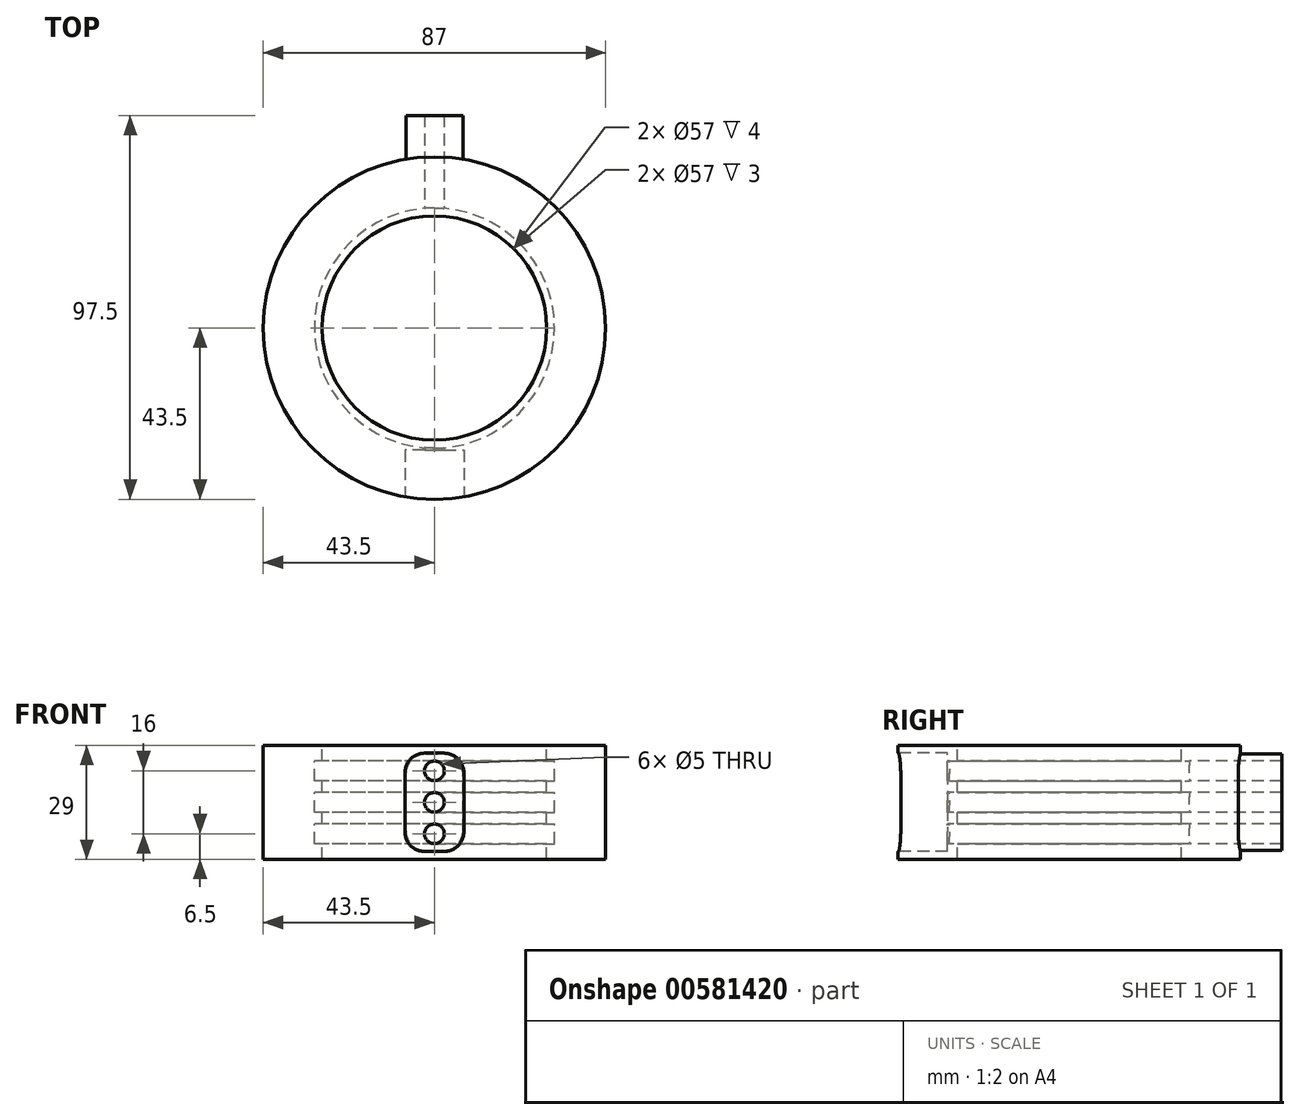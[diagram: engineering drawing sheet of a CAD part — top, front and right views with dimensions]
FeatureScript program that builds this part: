
annotation { "Feature Type Name" : "Feature", "Feature Type Description" : "" }
export const myFeature = defineFeature(function(context is Context, id is Id, definition is map)
    precondition{}
    {
        {
            var Q0;
            Q0=qCreatedBy(makeId("Front.planeOp"),FACE);
            var sketch = newSketch(context, id + "F0", { "sketchPlane" : qUnion([Q0])});
            skLineSegment(sketch, "E0.bottom", {"start": v(28.5, 14.5) * mm, "end": v(43.5, 14.5) * mm});
            skLineSegment(sketch, "E0.top", {"start": v(28.5, -14.5) * mm, "end": v(43.5, -14.5) * mm});
            skLineSegment(sketch, "E0.left", {"start": v(28.5, 14.5) * mm, "end": v(28.5, 10.5) * mm});
            skLineSegment(sketch, "E0.right", {"start": v(43.5, 14.5) * mm, "end": v(43.5, -14.5) * mm});
            skLineSegment(sketch, "E1", {"start": v(0, 16.26) * mm, "end": v(0, -13.74) * mm});
            skLineSegment(sketch, "E2", {"start": v(28.5, -14.5) * mm, "end": v(28.5, -10.5) * mm});
            skLineSegment(sketch, "E3", {"start": v(28.5, 2.5) * mm, "end": v(30.5, 2.5) * mm});
            skLineSegment(sketch, "E4", {"start": v(30.5, 2.5) * mm, "end": v(30.5, -2.5) * mm});
            skLineSegment(sketch, "E5", {"start": v(28.5, -2.5) * mm, "end": v(30.5, -2.5) * mm});
            skPoint(sketch, "E6.start.orphan", {"position": v(28.5, 0) * mm});
            skLineSegment(sketch, "E7", {"start": v(28.5, 5.5) * mm, "end": v(30.5, 5.5) * mm});
            skLineSegment(sketch, "E8", {"start": v(30.5, 5.5) * mm, "end": v(30.5, 5.5) * mm});
            skLineSegment(sketch, "E9", {"start": v(30.5, 5.5) * mm, "end": v(30.5, 10.5) * mm});
            skLineSegment(sketch, "E10", {"start": v(30.5, 10.5) * mm, "end": v(30.5, 10.5) * mm});
            skLineSegment(sketch, "E11", {"start": v(30.5, 10.5) * mm, "end": v(28.5, 10.5) * mm});
            skLineSegment(sketch, "E12", {"start": v(28.5, -5.5) * mm, "end": v(30.5, -5.5) * mm});
            skLineSegment(sketch, "E13", {"start": v(30.5, -5.5) * mm, "end": v(30.5, -10.5) * mm});
            skLineSegment(sketch, "E14", {"start": v(30.5, -10.5) * mm, "end": v(28.5, -10.5) * mm});
            skLineSegment(sketch, "E15.trimOffspring", {"start": v(28.5, -10.5) * mm, "end": v(28.5, -14.5) * mm});
            skLineSegment(sketch, "E16", {"start": v(28.5, 5.5) * mm, "end": v(28.5, 2.5) * mm});
            skLineSegment(sketch, "E17", {"start": v(28.5, -5.5) * mm, "end": v(28.5, -2.5) * mm});
            skSolve(sketch);
        }
        {
            var Q0;
            Q0=makeQuery(id+"F0.imprint","IMPRINT",FACE,{"disambiguationData":[TD([[makeQuery(id+"F0.imprint","IMPRINT",EDGE,{"derivedFrom":sQuery(id+"F0.wireOp",EDGE,"E0.bottom")}),-1.0]])]});
            var Q1;
            Q1=sQuery(id+"F0.wireOp",EDGE,"E1");
            revolve(context, id + "F1", {"entities" : qUnion([Q0]), "axis" : qUnion([Q1]), "revolveType" : RevolveType.FULL});
        }
        {
            var Q0;
            Q0=qCreatedBy(makeId("Front.planeOp"),FACE);
            cPlane(context, id + "F2", {"entities" : qUnion([Q0]), "cplaneType" : CPlaneType.OFFSET, "offset" : 43.5 * mm, "width" : 150 * mm, "height" : 150 * mm});
        }
        {
            var Q0;
            Q0=qCreatedBy(id+"F2.planeOp",FACE);
            var sketch = newSketch(context, id + "F3", { "sketchPlane" : qUnion([Q0])});
            skPoint(sketch, "E18", {"position": v(0, 0) * mm});
            skPoint(sketch, "E19", {"position": v(0, 8) * mm});
            skPoint(sketch, "E20", {"position": v(0, -8) * mm});
            skLineSegment(sketch, "E21.bottom", {"start": v(7.5, 12.5) * mm, "end": v(-7.5, 12.5) * mm});
            skLineSegment(sketch, "E21.top", {"start": v(7.5, -12.5) * mm, "end": v(-7.5, -12.5) * mm});
            skLineSegment(sketch, "E21.left", {"start": v(7.5, 12.5) * mm, "end": v(7.5, -12.5) * mm});
            skLineSegment(sketch, "E21.right", {"start": v(-7.5, 12.5) * mm, "end": v(-7.5, -12.5) * mm});
            skSolve(sketch);
        }
        {
            var Q0;
            Q0=makeQuery(id+"F3.imprint","IMPRINT",FACE,{"disambiguationData":[TD([[makeQuery(id+"F3.imprint","IMPRINT",EDGE,{"derivedFrom":sQuery(id+"F3.wireOp",EDGE,"E21.bottom")}),1.0]])]});
            extrude(context, id + "F4", {"entities" : qUnion([Q0]), "operationType" : NewBodyOperationType.REMOVE, "oppositeDirection" : true, "depth" : 12.5 * mm, "offsetDistance" : 25 * mm});
        }
        {
            var Q0;
            Q0=qCreatedBy(makeId("Front.planeOp"),FACE);
            cPlane(context, id + "F5", {"entities" : qUnion([Q0]), "cplaneType" : CPlaneType.OFFSET, "offset" : 40 * mm, "oppositeDirection" : true, "width" : 150 * mm, "height" : 150 * mm});
        }
        {
            var Q0;
            Q0=qCreatedBy(id+"F5.planeOp",FACE);
            var sketch = newSketch(context, id + "F6", { "sketchPlane" : qUnion([Q0])});
            skLineSegment(sketch, "E22.bottom", {"start": v(-7.25, 12.25) * mm, "end": v(7.25, 12.25) * mm});
            skLineSegment(sketch, "E22.top", {"start": v(-7.25, -12.25) * mm, "end": v(7.25, -12.25) * mm});
            skLineSegment(sketch, "E22.left", {"start": v(-7.25, 12.25) * mm, "end": v(-7.25, -12.25) * mm});
            skLineSegment(sketch, "E22.right", {"start": v(7.25, 12.25) * mm, "end": v(7.25, -12.25) * mm});
            skPoint(sketch, "E22.middle", {"position": v(0, 0) * mm});
            skSolve(sketch);
        }
        {
            var Q0;
            Q0=makeQuery(id+"F6.imprint","IMPRINT",FACE,{"disambiguationData":[TD([[makeQuery(id+"F6.imprint","IMPRINT",EDGE,{"derivedFrom":sQuery(id+"F6.wireOp",EDGE,"E22.bottom")}),-1.0]])]});
            extrude(context, id + "F7", {"entities" : qUnion([Q0]), "operationType" : NewBodyOperationType.ADD, "oppositeDirection" : true, "depth" : 14 * mm, "offsetDistance" : 25 * mm});
        }
        {
            var Q0;
            Q0=sQuery(id+"F3.wireOp",VERTEX,"E19");
            var Q1;
            Q1=sQuery(id+"F3.wireOp",VERTEX,"E18");
            var Q2;
            Q2=sQuery(id+"F3.wireOp",VERTEX,"E20");
            var Q3;
            Q3=makeQuery(id+"F1.opRevolve","SWEPT_BODY",BODY,{"disambiguationData":[OSD([sQuery(id+"F0.wireOp",EDGE,"E0.bottom"),sQuery(id+"F0.wireOp",EDGE,"E0.top"),sQuery(id+"F0.wireOp",EDGE,"E0.right"),sQuery(id+"F0.wireOp",EDGE,"E0.left"),sQuery(id+"F0.wireOp",EDGE,"E3"),sQuery(id+"F0.wireOp",EDGE,"E4"),sQuery(id+"F0.wireOp",EDGE,"E5"),sQuery(id+"F0.wireOp",EDGE,"E7"),sQuery(id+"F0.wireOp",EDGE,"E9"),sQuery(id+"F0.wireOp",EDGE,"E11"),sQuery(id+"F0.wireOp",EDGE,"E12"),sQuery(id+"F0.wireOp",EDGE,"E13"),sQuery(id+"F0.wireOp",EDGE,"E14"),sQuery(id+"F0.wireOp",EDGE,"E15.trimOffspring"),sQuery(id+"F0.wireOp",EDGE,"E16"),sQuery(id+"F0.wireOp",EDGE,"E17")])]});
            hole(context, id + "F8", {"style" : HoleStyle.SIMPLE, "endStyle" : HoleEndStyle.THROUGH, "holeDiameter" : 5 * mm, "majorDiameter" : 5 * mm, "isTappedThrough" : true, "tappedDepth" : 12 * mm, "tapClearance" : 3, "locations" : qUnion([Q0, Q1, Q2]), "scope" : qUnion([Q3])});
        }
        {
            var Q0;
            Q0=makeQuery(id+"F4.boolean.opBoolean","COPY",EDGE,{"derivedFrom":makeQuery(id+"F4.opExtrude","SWEPT_EDGE",EDGE,{"disambiguationData":[OSD([sQuery(id+"F3.wireOp",EDGE,"E21.bottom"),sQuery(id+"F3.wireOp",EDGE,"E21.right")])]})});
            var Q1;
            Q1=makeQuery(id+"F4.boolean.opBoolean","COPY",EDGE,{"derivedFrom":makeQuery(id+"F4.opExtrude","SWEPT_EDGE",EDGE,{"disambiguationData":[OSD([sQuery(id+"F3.wireOp",EDGE,"E21.bottom"),sQuery(id+"F3.wireOp",EDGE,"E21.left")])]})});
            var Q2;
            Q2=makeQuery(id+"F4.boolean.opBoolean","COPY",EDGE,{"derivedFrom":makeQuery(id+"F4.opExtrude","SWEPT_EDGE",EDGE,{"disambiguationData":[OSD([sQuery(id+"F3.wireOp",EDGE,"E21.top"),sQuery(id+"F3.wireOp",EDGE,"E21.right")])]})});
            var Q3;
            Q3=makeQuery(id+"F4.boolean.opBoolean","COPY",EDGE,{"derivedFrom":makeQuery(id+"F4.opExtrude","SWEPT_EDGE",EDGE,{"disambiguationData":[OSD([sQuery(id+"F3.wireOp",EDGE,"E21.top"),sQuery(id+"F3.wireOp",EDGE,"E21.left")])]})});
            var Q4;
            Q4=makeQuery(id+"F7.opExtrude","SWEPT_EDGE",EDGE,{"disambiguationData":[OSD([sQuery(id+"F6.wireOp",EDGE,"E22.bottom"),sQuery(id+"F6.wireOp",EDGE,"E22.right")])]});
            var Q5;
            Q5=makeQuery(id+"F7.opExtrude","SWEPT_EDGE",EDGE,{"disambiguationData":[OSD([sQuery(id+"F6.wireOp",EDGE,"E22.bottom"),sQuery(id+"F6.wireOp",EDGE,"E22.left")])]});
            var Q6;
            Q6=makeQuery(id+"F7.opExtrude","SWEPT_EDGE",EDGE,{"disambiguationData":[OSD([sQuery(id+"F6.wireOp",EDGE,"E22.top"),sQuery(id+"F6.wireOp",EDGE,"E22.right")])]});
            var Q7;
            Q7=makeQuery(id+"F7.opExtrude","SWEPT_EDGE",EDGE,{"disambiguationData":[OSD([sQuery(id+"F6.wireOp",EDGE,"E22.top"),sQuery(id+"F6.wireOp",EDGE,"E22.left")])]});
            fillet(context, id + "F9", {"entities" : qUnion([Q0, Q1, Q2, Q3, Q4, Q5, Q6, Q7]), "radius" : 5 * mm, "tangentPropagation" : true, "allowEdgeOverflow" : false});
        }
    });
